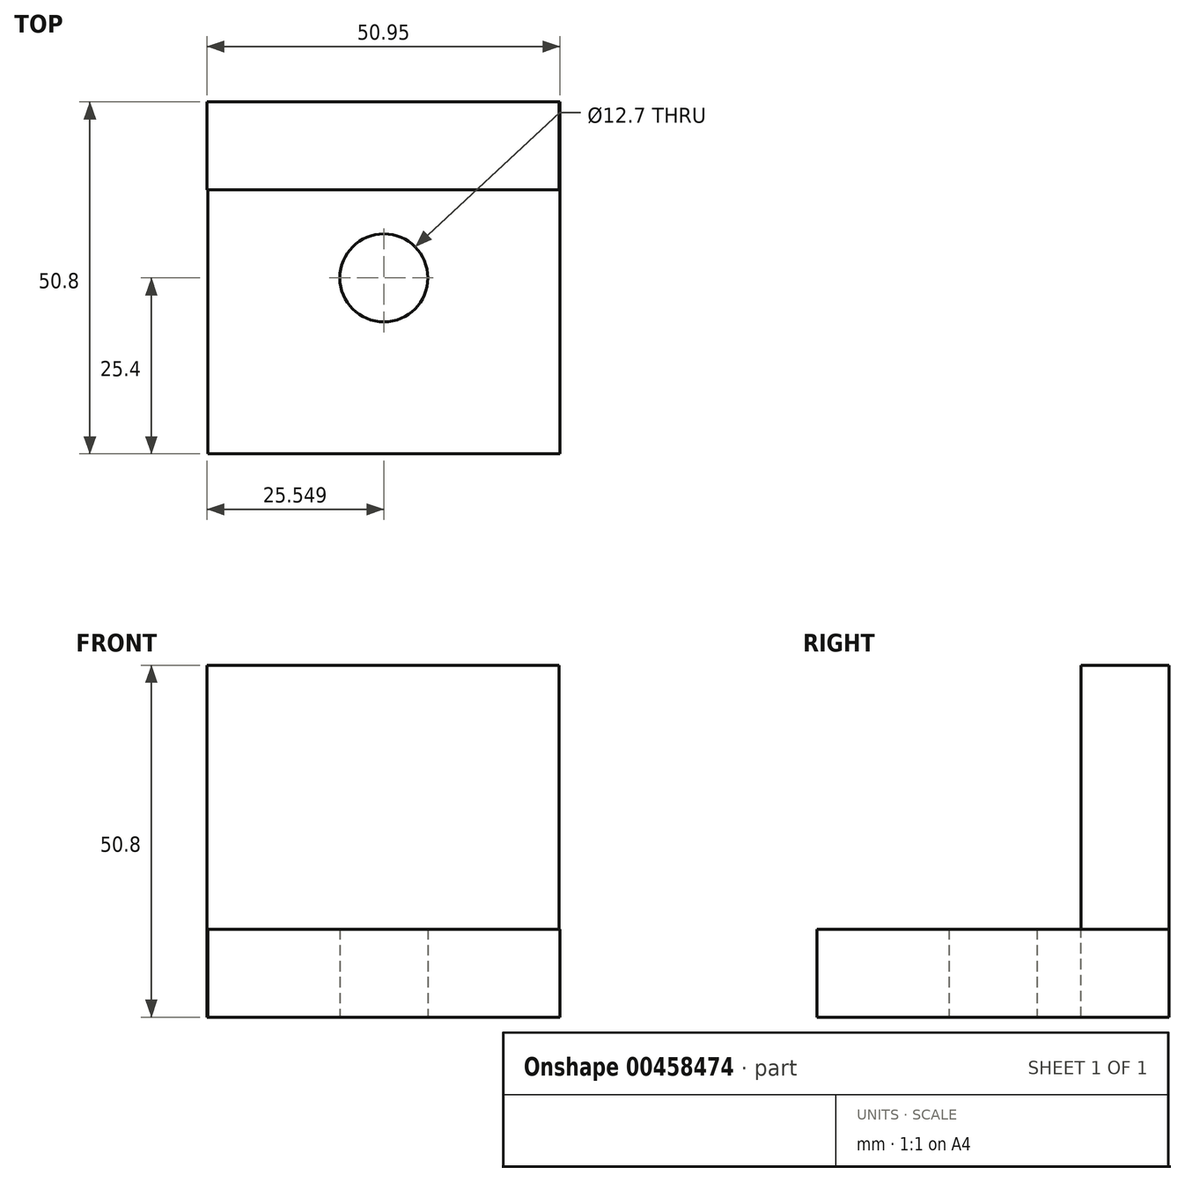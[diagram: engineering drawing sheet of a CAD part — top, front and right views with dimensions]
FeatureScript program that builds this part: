
annotation { "Feature Type Name" : "Feature", "Feature Type Description" : "" }
export const myFeature = defineFeature(function(context is Context, id is Id, definition is map)
    precondition{}
    {
        {
            var Q0;
            Q0=qCreatedBy(makeId("Top.planeOp"),FACE);
            var sketch = newSketch(context, id + "F0", { "sketchPlane" : qUnion([Q0])});
            skLineSegment(sketch, "E0", {"start": v(-62.33, 0) * mm, "end": v(-11.53, 0) * mm});
            skLineSegment(sketch, "E1", {"start": v(-11.53, 0) * mm, "end": v(-11.53, -50.8) * mm});
            skLineSegment(sketch, "E2", {"start": v(-11.53, -50.8) * mm, "end": v(-62.33, -50.8) * mm});
            skLineSegment(sketch, "E3", {"start": v(-62.33, -50.8) * mm, "end": v(-62.33, 0) * mm});
            skPoint(sketch, "E4.centerSnap0", {"position": v(-36.93, 0) * mm});
            skCircle(sketch, "E5", {"center": v(-36.93, -25.4) * mm, "radius": 6.35 * mm});
            skPoint(sketch, "E5.centerSnap0", {"position": v(-36.93, -50.8) * mm});
            skPoint(sketch, "E5.centerSnap1", {"position": v(-11.53, -25.4) * mm});
            skSolve(sketch);
        }
        {
            var Q0;
            Q0=makeQuery(id+"F0.imprint","IMPRINT",FACE,{"disambiguationData":[TD([[makeQuery(id+"F0.imprint","IMPRINT",EDGE,{"derivedFrom":sQuery(id+"F0.wireOp",EDGE,"E0")}),-1.0]])]});
            extrude(context, id + "F1", {"entities" : qUnion([Q0]), "depth" : 12.7 * mm});
        }
        {
            var Q0;
            Q0=qCreatedBy(makeId("Front.planeOp"),FACE);
            var sketch = newSketch(context, id + "F2", { "sketchPlane" : qUnion([Q0])});
            skLineSegment(sketch, "E6", {"start": v(-62.48, 0) * mm, "end": v(-62.48, 50.8) * mm});
            skLineSegment(sketch, "E7", {"start": v(-62.48, 0) * mm, "end": v(-11.68, 0) * mm});
            skLineSegment(sketch, "E8", {"start": v(-11.68, 0) * mm, "end": v(-11.68, 50.8) * mm});
            skLineSegment(sketch, "E9", {"start": v(-11.68, 50.8) * mm, "end": v(-62.48, 50.8) * mm});
            skPoint(sketch, "E10.centerSnap0", {"position": v(-37.08, 0) * mm});
            skSolve(sketch);
        }
        {
            var Q0;
            Q0=makeQuery(id+"F2.imprint","IMPRINT",FACE,{"disambiguationData":[TD([[makeQuery(id+"F2.imprint","IMPRINT",EDGE,{"derivedFrom":sQuery(id+"F2.wireOp",EDGE,"E6")}),-1.0]])]});
            extrude(context, id + "F3", {"entities" : qUnion([Q0]), "operationType" : NewBodyOperationType.ADD, "depth" : 12.7 * mm});
        }
    });
